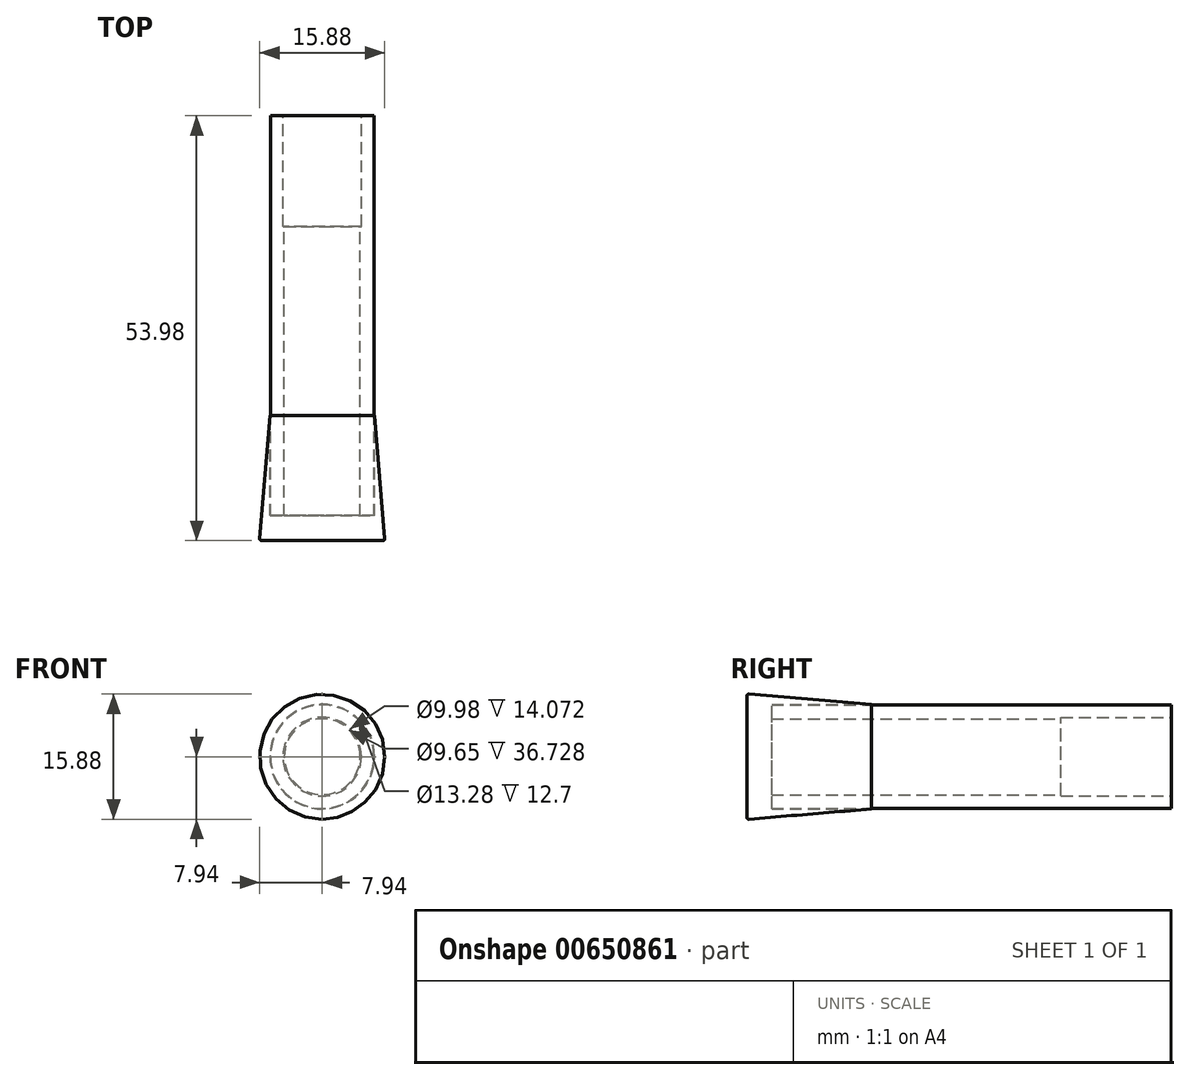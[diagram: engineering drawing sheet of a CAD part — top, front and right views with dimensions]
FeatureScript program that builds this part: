
annotation { "Feature Type Name" : "Feature", "Feature Type Description" : "" }
export const myFeature = defineFeature(function(context is Context, id is Id, definition is map)
    precondition{}
    {
        {
            var Q0;
            Q0=qCreatedBy(makeId("Front.planeOp"),FACE);
            var sketch = newSketch(context, id + "F0", { "sketchPlane" : qUnion([Q0])});
            skCircle(sketch, "E0", {"center": v(0, 0) * mm, "radius": 6.58 * mm});
            skCircle(sketch, "E1", {"center": v(0, 0) * mm, "radius": 5 * mm});
            skSolve(sketch);
        }
        {
            var Q0;
            Q0=makeQuery(id+"F0.imprint","IMPRINT",FACE,{"disambiguationData":[TD([[makeQuery(id+"F0.imprint","IMPRINT",EDGE,{"derivedFrom":sQuery(id+"F0.wireOp",EDGE,"E0")}),1.0]])]});
            extrude(context, id + "F1", {"entities" : qUnion([Q0]), "depth" : 14.07 * mm, "offsetDistance" : 25.4 * mm});
        }
        {
            var Q0;
            Q0=qCreatedBy(makeId("Front.planeOp"),FACE);
            var sketch = newSketch(context, id + "F2", { "sketchPlane" : qUnion([Q0])});
            skCircle(sketch, "E2", {"center": v(0, 0) * mm, "radius": 6.58 * mm});
            skCircle(sketch, "E3", {"center": v(0, 0) * mm, "radius": 4.83 * mm});
            skSolve(sketch);
        }
        {
            var Q0;
            Q0 = qSketchRegion(id + "F2", true);
            extrude(context, id + "F3", {"entities" : qUnion([Q0]), "operationType" : NewBodyOperationType.ADD, "depth" : 50.8 * mm, "offsetDistance" : 25.4 * mm, "hasSecondDirection" : true, "secondDirectionOppositeDirection" : false, "secondDirectionDepth" : 14.07 * mm});
        }
        {
            var Q0;
            Q0=qCreatedBy(makeId("Front.planeOp"),FACE);
            var sketch = newSketch(context, id + "F4", { "sketchPlane" : qUnion([Q0])});
            skCircle(sketch, "E4", {"center": v(0, 0) * mm, "radius": 8.23 * mm});
            skCircle(sketch, "E5", {"center": v(0, 0) * mm, "radius": 6.64 * mm});
            skSolve(sketch);
        }
        {
            var Q0;
            Q0 = qSketchRegion(id + "F4", true);
            extrude(context, id + "F5", {"entities" : qUnion([Q0]), "depth" : 50.8 * mm, "offsetDistance" : 25.4 * mm, "hasSecondDirection" : true, "secondDirectionOppositeDirection" : false, "secondDirectionDepth" : 38.1 * mm});
        }
        {
            var Q0;
            Q0=qCreatedBy(makeId("Front.planeOp"),FACE);
            var sketch = newSketch(context, id + "F6", { "sketchPlane" : qUnion([Q0])});
            skCircle(sketch, "E6", {"center": v(0, 0) * mm, "radius": 8.23 * mm});
            skSolve(sketch);
        }
        {
            var Q0;
            Q0 = qSketchRegion(id + "F6", true);
            extrude(context, id + "F7", {"entities" : qUnion([Q0]), "operationType" : NewBodyOperationType.ADD, "depth" : 53.97 * mm, "offsetDistance" : 25.4 * mm, "hasSecondDirection" : true, "secondDirectionOppositeDirection" : false, "secondDirectionDepth" : 50.8 * mm});
        }
        {
            var Q0;
            Q0=makeQuery(id+"F5.opExtrude","CAP_EDGE",EDGE,{"disambiguationData":[OSD([sQuery(id+"F4.wireOp",EDGE,"E4")])],"isStart":true});
            chamfer(context, id + "F8", {"entities" : qUnion([Q0]), "chamferType" : ChamferType.TWO_OFFSETS, "width1" : 19.05 * mm, "oppositeDirection" : false, "width2" : 1.59 * mm, "tangentPropagation" : true});
        }
        {
            var Q0;
            Q0=makeQuery(id+"F7.opExtrude","CAP_FACE",FACE,{"disambiguationData":[OSD([sQuery(id+"F6.wireOp",EDGE,"E6")])],"isStart":false});
            fillet(context, id + "F9", {"entities" : qUnion([Q0]), "radius" : 0.25 * mm, "tangentPropagation" : true, "allowEdgeOverflow" : false});
        }
    });
